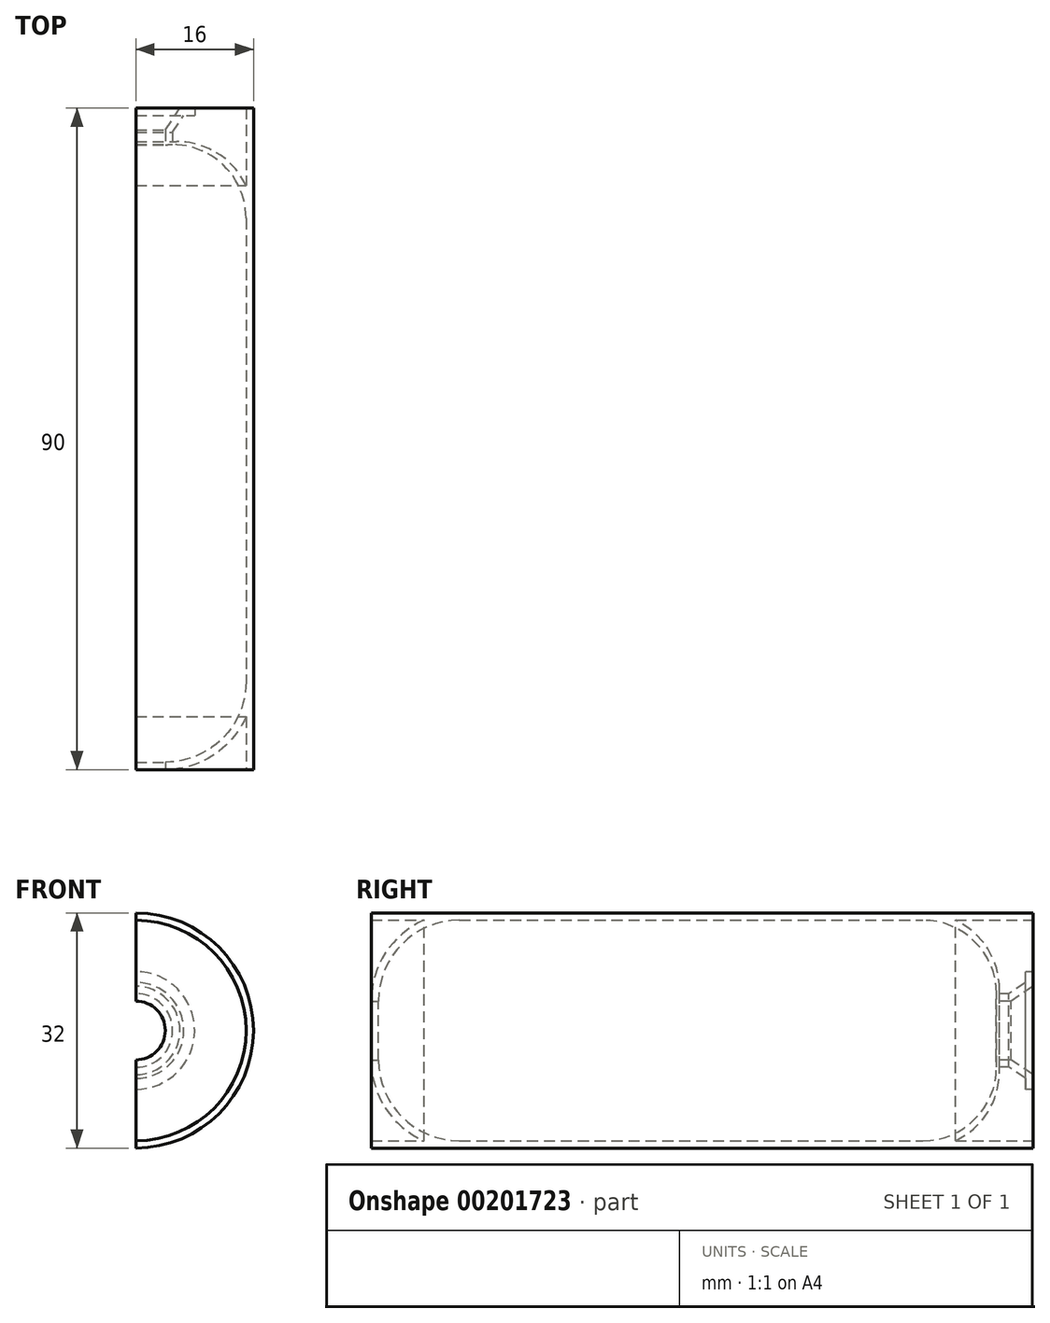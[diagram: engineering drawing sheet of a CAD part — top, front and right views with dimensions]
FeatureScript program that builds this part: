
annotation { "Feature Type Name" : "Feature", "Feature Type Description" : "" }
export const myFeature = defineFeature(function(context is Context, id is Id, definition is map)
    precondition{}
    {
        {
            var Q0;
            Q0=qCreatedBy(makeId("Right.planeOp"),FACE);
            var sketch = newSketch(context, id + "F0", { "sketchPlane" : qUnion([Q0])});
            skLineSegment(sketch, "E0.bottom", {"start": v(-3.13, 33.38) * mm, "end": v(86.87, 33.38) * mm});
            skLineSegment(sketch, "E0.top", {"start": v(-3.13, 32.38) * mm, "end": v(4.08, 32.38) * mm});
            skLineSegment(sketch, "E0.left", {"start": v(-3.13, 33.38) * mm, "end": v(-3.13, 32.38) * mm});
            skLineSegment(sketch, "E0.right", {"start": v(86.87, 33.38) * mm, "end": v(86.87, 32.38) * mm});
            skPoint(sketch, "E0.middle", {"position": v(41.87, 32.88) * mm});
            skLineSegment(sketch, "E1.bottom", {"start": v(86.87, 32.38) * mm, "end": v(81.87, 32.38) * mm, "construction": true});
            skLineSegment(sketch, "E1.top", {"start": v(86.87, 21.38) * mm, "end": v(85.87, 21.38) * mm});
            skLineSegment(sketch, "E1.left", {"start": v(86.87, 32.38) * mm, "end": v(86.87, 21.38) * mm, "construction": true});
            skLineSegment(sketch, "E1.right", {"start": v(81.87, 32.38) * mm, "end": v(81.87, 21.38) * mm, "construction": true});
            skLineSegment(sketch, "E2.bottom", {"start": v(81.87, 32.38) * mm, "end": v(71.87, 32.38) * mm, "construction": true});
            skLineSegment(sketch, "E2.top", {"start": v(81.87, 21.38) * mm, "end": v(71.87, 21.38) * mm, "construction": true});
            skLineSegment(sketch, "E2.right", {"start": v(71.87, 33.38) * mm, "end": v(71.87, 21.38) * mm, "construction": true});
            skLineSegment(sketch, "E3.0", {"start": v(85.87, 22.38) * mm, "end": v(85.37, 22.38) * mm, "construction": true});
            skLineSegment(sketch, "E4.0", {"start": v(85.87, 32.38) * mm, "end": v(85.87, 21.38) * mm, "construction": true});
            skArc(sketch, "E5", {"start": v(82.3, 22.38) * mm, "mid": v(80.84, 28.3) * mm, "end": v(76.33, 32.38) * mm});
            skArc(sketch, "E6", {"start": v(81.87, 21.38) * mm, "mid": v(79.3, 29.1) * mm, "end": v(71.87, 32.38) * mm});
            skLineSegment(sketch, "E7.trimOffspring", {"start": v(76.33, 32.38) * mm, "end": v(86.87, 32.38) * mm});
            skLineSegment(sketch, "E8.top", {"start": v(86.87, 25.38) * mm, "end": v(85.87, 25.38) * mm});
            skLineSegment(sketch, "E8.left", {"start": v(86.87, 23.38) * mm, "end": v(86.87, 25.38) * mm});
            skLineSegment(sketch, "E8.right", {"start": v(85.87, 22.38) * mm, "end": v(85.87, 22.72) * mm, "construction": true});
            skLineSegment(sketch, "E9.bottom", {"start": v(-3.13, 32.38) * mm, "end": v(-2.13, 32.38) * mm, "construction": true});
            skLineSegment(sketch, "E9.top", {"start": v(-3.13, 21.38) * mm, "end": v(-2.13, 21.38) * mm});
            skLineSegment(sketch, "E9.left", {"start": v(-3.13, 32.38) * mm, "end": v(-3.13, 21.38) * mm, "construction": true});
            skLineSegment(sketch, "E9.right", {"start": v(-2.13, 32.38) * mm, "end": v(-2.13, 21.38) * mm, "construction": true});
            skLineSegment(sketch, "E10.bottom", {"start": v(-2.13, 32.38) * mm, "end": v(4.08, 32.38) * mm, "construction": true});
            skLineSegment(sketch, "E10.top", {"start": v(-2.13, 33.38) * mm, "end": v(8.87, 33.38) * mm, "construction": true});
            skLineSegment(sketch, "E10.left", {"start": v(-2.13, 32.38) * mm, "end": v(-2.13, 33.38) * mm, "construction": true});
            skLineSegment(sketch, "E10.right", {"start": v(8.87, 32.38) * mm, "end": v(8.87, 33.38) * mm, "construction": true});
            skArc(sketch, "E11", {"start": v(4.08, 32.38) * mm, "mid": v(-1.17, 27.96) * mm, "end": v(-3.13, 21.38) * mm});
            skArc(sketch, "E12", {"start": v(8.87, 32.38) * mm, "mid": v(1.1, 29.16) * mm, "end": v(-2.13, 21.38) * mm});
            skLineSegment(sketch, "E13.trimOffspring", {"start": v(8.87, 32.38) * mm, "end": v(71.87, 32.38) * mm});
            skLineSegment(sketch, "E14", {"start": v(8.87, 21.38) * mm, "end": v(71.87, 21.38) * mm, "construction": true});
            skLineSegment(sketch, "E15.0", {"start": v(8.87, 17.38) * mm, "end": v(71.87, 17.38) * mm, "construction": true});
            skLineSegment(sketch, "E16.0", {"start": v(86.87, 23.38) * mm, "end": v(85.87, 23.38) * mm, "construction": true});
            skLineSegment(sketch, "E17.0", {"start": v(83.87, 21.38) * mm, "end": v(83.87, 25.38) * mm, "construction": true});
            skLineSegment(sketch, "E18", {"start": v(86.87, 23.38) * mm, "end": v(83.87, 21.38) * mm});
            skLineSegment(sketch, "E19.0", {"start": v(85.87, 23.92) * mm, "end": v(83.57, 22.38) * mm});
            skLineSegment(sketch, "E20.trimOffspring", {"start": v(83.87, 21.38) * mm, "end": v(81.87, 21.38) * mm});
            skLineSegment(sketch, "E21.trimOffspring", {"start": v(83.57, 22.38) * mm, "end": v(82.3, 22.38) * mm});
            skLineSegment(sketch, "E22.trimOffspring", {"start": v(85.87, 23.92) * mm, "end": v(85.87, 25.38) * mm});
            skSolve(sketch);
        }
        {
            var Q0;
            Q0=makeQuery(id+"F0.imprint","IMPRINT",FACE,{"disambiguationData":[TD([[makeQuery(id+"F0.imprint","IMPRINT",EDGE,{"derivedFrom":sQuery(id+"F0.wireOp",EDGE,"E0.bottom")}),-1.0]])]});
            var Q1;
            {var subQ5=sQuery(id+"F0.wireOp",EDGE,"E8.bottom");Q1=makeQuery(id+"F0.imprint","IMPRINT",FACE,{"disambiguationData":[TD([[makeQuery(id+"F0.imprint","IMPRINT",EDGE,{"derivedFrom":subQ5}),-1.0]])]});}
            var Q2;
            {var subQ5=sQuery(id+"F0.wireOp",EDGE,"E8.top");Q2=makeQuery(id+"F0.imprint","IMPRINT",FACE,{"disambiguationData":[TD([[makeQuery(id+"F0.imprint","IMPRINT",EDGE,{"derivedFrom":subQ5}),1.0]])]});}
            var Q3;
            Q3=sQuery(id+"F0.wireOp",EDGE,"E15.0");
            revolve(context, id + "F1", {"entities" : qUnion([Q0, Q1, Q2]), "axis" : qUnion([Q3]), "revolveType" : RevolveType.ONE_DIRECTION, "angle" : 180 * degree});
        }
    });
